# Revit family: Shower-Showerhead_Kit-KALLISTA-CENTRAL_PARK_WEST-P21386_1
name_source: partatom
category: Plumbing Fixtures
units: mm (PartAtom-declared; Revit-internal decimal feet)

## family parameters
Cut with Voids When Loaded = No
Host = Face
Maintain Annotation Orientation = No
OmniClass Number = 23.31.11.00
OmniClass Title = Faucets
Part Type = Normal
Room Calculation Point = No
Round Connector Dimension = Use Diameter
Shared = No

## types (6) — shared parameters
ADA Compliant = No
Assembly Code = D2010
CW Connection = No
Cold Water Inlet = Cold Water Inlet
Date Modified = 06/07/2022
Default Elevation = 72"
Description = Showerhead With Arm
Drain Included = No
Flow Rate = 2 GPM
HW Connection = Yes
Height = 4 7/16"
Hot Water Inlet = Hot Water Inlet
Length = 7 11/16"
Manufacturer = Kallista Co.
Master Format 2014 = 22 41 39
Master Format 2014 Name = Residential Faucets, Supplies, and Trim
Material = Premium Metal Construction
Pressure = 80.00 psi
Product Documentation Link = https://resources.kohler.com
Product Name = Centra Park West
Product Page URL = https://www.kallista.com
Tempered Water Inlet = Tempered Water Inlet
URL = https://www.kallista.com
Vent Connection = No
Waste Connection = No
Waste Water Outlet = Waste Water Outlet
WaterSense Certified = Yes
Width = 2 3/8"

## per-type parameters (varying)
| type | Finish | Model | Type |
| CP-Chrome | Kallista-Metal-CP-Chrome | P21386-00-CP | 1 |
| ULB-Unlaquered Brass | Kallista-Metal-ULB-Unlaquered_Brass | P21386-00-ULB | 2 |
| SN-Polished Nickel | Kallista-Metal-SN-Polished_Nickel | P21386-00-SN | 3 |
| BV-Brushed Bronze | Kallista-Metal-BV-Brushed_Bronze | P21386-00-BV | 4 |
| BN-Brushed Nickel | Kallista-Metal-BN-Brushed_Nickel | P21386-00-BN | 5 |
| BAF-Brushed French Gold | Kallista-Metal-BAF-Brushed_French_Gold | P21386-00-BAF | 6 |

## geometry (parser evidence)
native form markers: Sweep x6
no freeform markers — native parametric forms only
